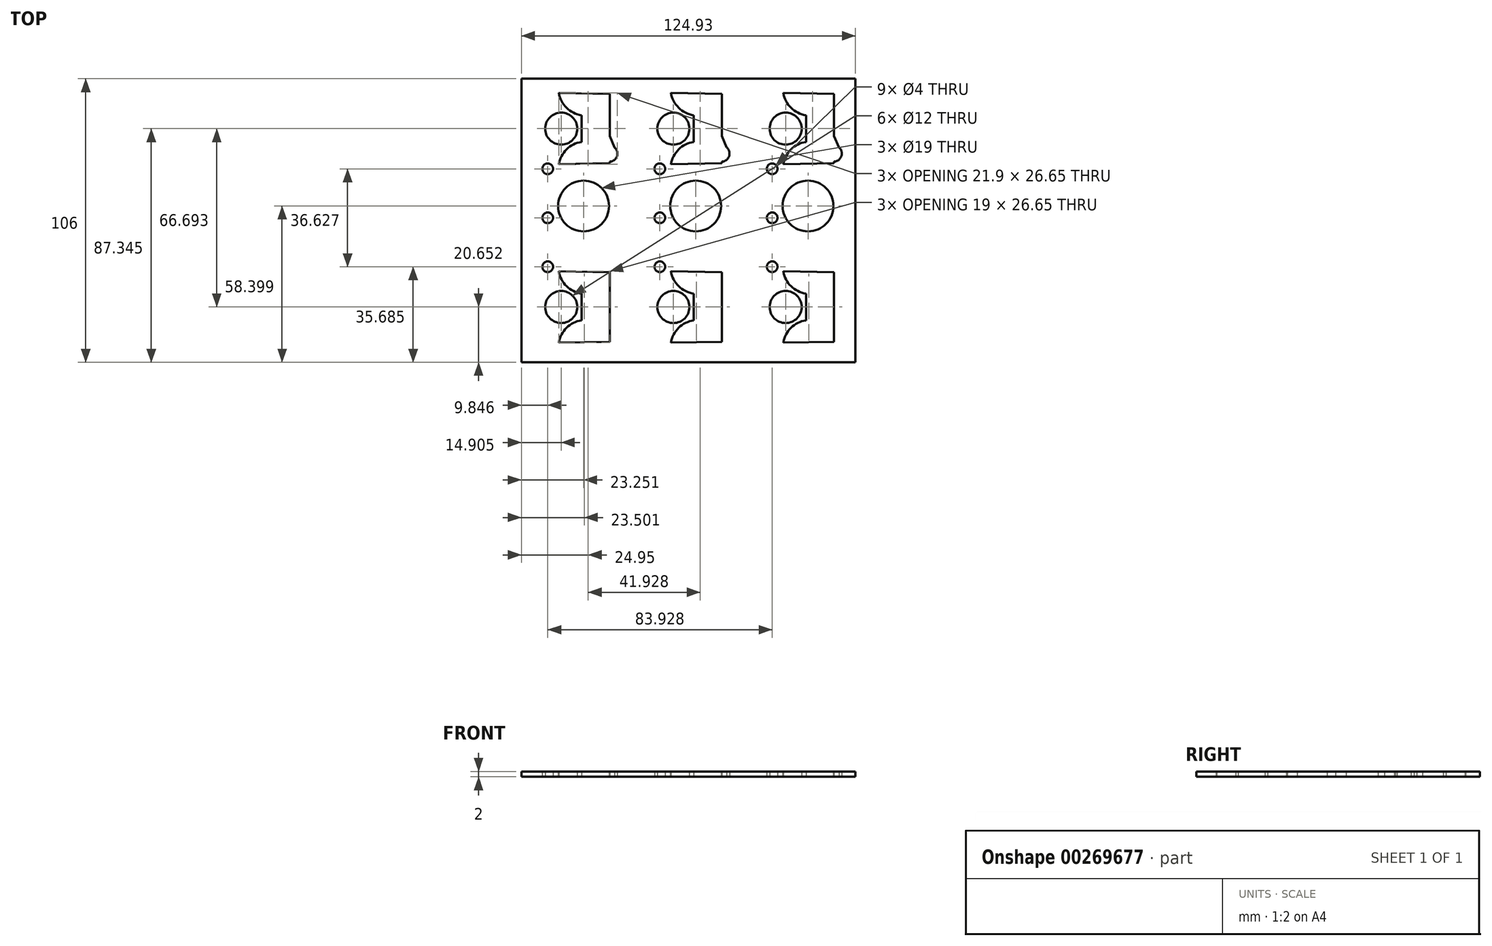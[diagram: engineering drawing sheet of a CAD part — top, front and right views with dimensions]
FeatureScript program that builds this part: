
annotation { "Feature Type Name" : "Feature", "Feature Type Description" : "" }
export const myFeature = defineFeature(function(context is Context, id is Id, definition is map)
    precondition{}
    {
        {
            var Q0;
            Q0=qCreatedBy(makeId("Top.planeOp"),FACE);
            var sketch = newSketch(context, id + "F0", { "sketchPlane" : qUnion([Q0])});
            skLineSegment(sketch, "E0.bottom", {"start": v(-21.33, 48.69) * mm, "end": v(19.67, 48.69) * mm});
            skLineSegment(sketch, "E0.top", {"start": v(-21.33, -57.31) * mm, "end": v(19.67, -57.31) * mm});
            skLineSegment(sketch, "E0.left", {"start": v(-21.33, 48.69) * mm, "end": v(-21.33, -57.31) * mm});
            skLineSegment(sketch, "E0.right", {"start": v(19.67, 48.69) * mm, "end": v(19.67, -57.31) * mm});
            skArc(sketch, "E1", {"start": v(-7.33, 43.36) * mm, "mid": v(-4.44, 37.81) * mm, "end": v(1.17, 35.04) * mm});
            skLineSegment(sketch, "E2", {"start": v(1.17, 35.04) * mm, "end": v(1.17, 25.04) * mm});
            skLineSegment(sketch, "E3", {"start": v(-11.51, 30.04) * mm, "end": v(22.8, 30.04) * mm, "construction": true});
            skArc(sketch, "E4.MirrorCS", {"start": v(-7.33, 16.71) * mm, "mid": v(-4.44, 22.26) * mm, "end": v(1.17, 25.04) * mm});
            skCircle(sketch, "E5", {"center": v(-1.94, 38.54) * mm, "radius": 1.5 * mm});
            skCircle(sketch, "E6.MirrorC", {"center": v(-1.94, 21.54) * mm, "radius": 1.5 * mm});
            skCircle(sketch, "E7", {"center": v(-6.43, 30.04) * mm, "radius": 6 * mm});
            skLineSegment(sketch, "E8", {"start": v(-27.8, -3.31) * mm, "end": v(21.21, -3.31) * mm, "construction": true});
            skCircle(sketch, "E9.MirrorC", {"center": v(-1.94, -28.16) * mm, "radius": 1.5 * mm});
            skArc(sketch, "E10.MirrorCS", {"start": v(-7.33, -23.33) * mm, "mid": v(-4.44, -28.88) * mm, "end": v(1.17, -31.66) * mm});
            skLineSegment(sketch, "E11.MirrorCS", {"start": v(1.17, -41.66) * mm, "end": v(1.17, -31.66) * mm});
            skArc(sketch, "E12.MirrorCS", {"start": v(-7.33, -49.98) * mm, "mid": v(-4.44, -44.43) * mm, "end": v(1.17, -41.66) * mm});
            skCircle(sketch, "E13.MirrorC", {"center": v(-1.94, -45.16) * mm, "radius": 1.5 * mm});
            skCircle(sketch, "E14.MirrorC", {"center": v(-6.43, -36.66) * mm, "radius": 6 * mm});
            skLineSegment(sketch, "E15", {"start": v(-4.58, -20.4) * mm, "end": v(-4.58, -51.53) * mm, "construction": true});
            skLineSegment(sketch, "E16", {"start": v(11.67, -23.7) * mm, "end": v(11.67, -49.7) * mm});
            skLineSegment(sketch, "E17", {"start": v(11.67, -49.7) * mm, "end": v(-7.33, -49.98) * mm});
            skLineSegment(sketch, "E18", {"start": v(11.67, -23.7) * mm, "end": v(-7.33, -23.33) * mm});
            skLineSegment(sketch, "E19.MirrorCS", {"start": v(11.67, 17.07) * mm, "end": v(-7.33, 16.71) * mm});
            skLineSegment(sketch, "E20.MirrorCS", {"start": v(11.67, 17.07) * mm, "end": v(11.67, 43.07) * mm});
            skLineSegment(sketch, "E21.MirrorCS", {"start": v(11.67, 43.07) * mm, "end": v(-7.33, 43.36) * mm});
            skCircle(sketch, "E22", {"center": v(1.92, 1.09) * mm, "radius": 9.5 * mm});
            skCircle(sketch, "E23", {"center": v(8.67, 26.69) * mm, "radius": 3 * mm});
            skCircle(sketch, "E24", {"center": v(11.57, 20.69) * mm, "radius": 3 * mm});
            skCircle(sketch, "E25", {"center": v(-11.49, -3.31) * mm, "radius": 2 * mm});
            skCircle(sketch, "E26", {"center": v(-11.49, -21.63) * mm, "radius": 2 * mm});
            skCircle(sketch, "E27.MirrorC", {"center": v(-11.49, 15) * mm, "radius": 2 * mm});
            skLineSegment(sketch, "E28", {"start": v(6.28, 24.87) * mm, "end": v(8.86, 19.4) * mm});
            skLineSegment(sketch, "E29", {"start": v(13.53, 22.96) * mm, "end": v(11.43, 27.87) * mm});
            skLineSegment(sketch, "E30.bottom", {"start": v(20.67, 48.69) * mm, "end": v(61.67, 48.69) * mm});
            skLineSegment(sketch, "E30.top", {"start": v(20.67, -57.31) * mm, "end": v(61.67, -57.31) * mm});
            skLineSegment(sketch, "E30.left", {"start": v(20.67, 48.69) * mm, "end": v(20.67, -57.31) * mm});
            skLineSegment(sketch, "E30.right", {"start": v(61.67, 48.69) * mm, "end": v(61.67, -57.31) * mm});
            skArc(sketch, "E31", {"start": v(34.67, 43.36) * mm, "mid": v(37.56, 37.81) * mm, "end": v(43.17, 35.04) * mm});
            skLineSegment(sketch, "E32", {"start": v(43.17, 35.04) * mm, "end": v(43.17, 25.04) * mm});
            skLineSegment(sketch, "E33", {"start": v(30.49, 30.04) * mm, "end": v(64.8, 30.04) * mm, "construction": true});
            skArc(sketch, "E34.MirrorCS", {"start": v(34.67, 16.71) * mm, "mid": v(37.56, 22.26) * mm, "end": v(43.17, 25.04) * mm});
            skCircle(sketch, "E35", {"center": v(40.06, 38.54) * mm, "radius": 1.5 * mm});
            skCircle(sketch, "E36.MirrorC", {"center": v(40.06, 21.54) * mm, "radius": 1.5 * mm});
            skCircle(sketch, "E37", {"center": v(35.57, 30.04) * mm, "radius": 6 * mm});
            skLineSegment(sketch, "E38", {"start": v(14.2, -3.31) * mm, "end": v(63.21, -3.31) * mm, "construction": true});
            skCircle(sketch, "E39.MirrorC", {"center": v(40.06, -28.16) * mm, "radius": 1.5 * mm});
            skArc(sketch, "E40.MirrorCS", {"start": v(34.67, -23.33) * mm, "mid": v(37.56, -28.88) * mm, "end": v(43.17, -31.66) * mm});
            skLineSegment(sketch, "E41.MirrorCS", {"start": v(43.17, -41.66) * mm, "end": v(43.17, -31.66) * mm});
            skArc(sketch, "E42.MirrorCS", {"start": v(34.67, -49.98) * mm, "mid": v(37.56, -44.43) * mm, "end": v(43.17, -41.66) * mm});
            skCircle(sketch, "E43.MirrorC", {"center": v(40.06, -45.16) * mm, "radius": 1.5 * mm});
            skCircle(sketch, "E44.MirrorC", {"center": v(35.57, -36.66) * mm, "radius": 6 * mm});
            skLineSegment(sketch, "E45", {"start": v(37.42, -20.4) * mm, "end": v(37.42, -51.53) * mm, "construction": true});
            skLineSegment(sketch, "E46", {"start": v(53.67, -23.7) * mm, "end": v(53.67, -49.7) * mm});
            skLineSegment(sketch, "E47", {"start": v(53.67, -49.7) * mm, "end": v(34.67, -49.98) * mm});
            skLineSegment(sketch, "E48", {"start": v(53.67, -23.7) * mm, "end": v(34.67, -23.33) * mm});
            skLineSegment(sketch, "E49.MirrorCS", {"start": v(53.67, 17.07) * mm, "end": v(34.67, 16.71) * mm});
            skLineSegment(sketch, "E50.MirrorCS", {"start": v(53.67, 17.07) * mm, "end": v(53.67, 43.07) * mm});
            skLineSegment(sketch, "E51.MirrorCS", {"start": v(53.67, 43.07) * mm, "end": v(34.67, 43.36) * mm});
            skCircle(sketch, "E52", {"center": v(43.92, 1.09) * mm, "radius": 9.5 * mm});
            skCircle(sketch, "E53", {"center": v(50.67, 26.69) * mm, "radius": 3 * mm});
            skCircle(sketch, "E54", {"center": v(53.57, 20.69) * mm, "radius": 3 * mm});
            skCircle(sketch, "E55", {"center": v(30.51, -3.31) * mm, "radius": 2 * mm});
            skCircle(sketch, "E56", {"center": v(30.51, -21.63) * mm, "radius": 2 * mm});
            skCircle(sketch, "E57.MirrorC", {"center": v(30.51, 15) * mm, "radius": 2 * mm});
            skLineSegment(sketch, "E58", {"start": v(48.28, 24.87) * mm, "end": v(50.86, 19.4) * mm});
            skLineSegment(sketch, "E59", {"start": v(55.53, 22.96) * mm, "end": v(53.43, 27.87) * mm});
            skLineSegment(sketch, "E60.bottom", {"start": v(-63.26, 48.69) * mm, "end": v(-22.26, 48.69) * mm});
            skLineSegment(sketch, "E60.top", {"start": v(-63.26, -57.31) * mm, "end": v(-22.26, -57.31) * mm});
            skLineSegment(sketch, "E60.left", {"start": v(-63.26, 48.69) * mm, "end": v(-63.26, -57.31) * mm});
            skLineSegment(sketch, "E60.right", {"start": v(-22.26, 48.69) * mm, "end": v(-22.26, -57.31) * mm});
            skArc(sketch, "E61", {"start": v(-49.26, 43.36) * mm, "mid": v(-46.37, 37.81) * mm, "end": v(-40.76, 35.04) * mm});
            skLineSegment(sketch, "E62", {"start": v(-40.76, 35.04) * mm, "end": v(-40.76, 25.04) * mm});
            skLineSegment(sketch, "E63", {"start": v(-53.44, 30.04) * mm, "end": v(-19.13, 30.04) * mm, "construction": true});
            skArc(sketch, "E64.MirrorCS", {"start": v(-49.26, 16.71) * mm, "mid": v(-46.37, 22.26) * mm, "end": v(-40.76, 25.04) * mm});
            skCircle(sketch, "E65", {"center": v(-43.87, 38.54) * mm, "radius": 1.5 * mm});
            skCircle(sketch, "E66.MirrorC", {"center": v(-43.87, 21.54) * mm, "radius": 1.5 * mm});
            skCircle(sketch, "E67", {"center": v(-48.35, 30.04) * mm, "radius": 6 * mm});
            skLineSegment(sketch, "E68", {"start": v(-69.73, -3.31) * mm, "end": v(-20.72, -3.31) * mm, "construction": true});
            skCircle(sketch, "E69.MirrorC", {"center": v(-43.87, -28.16) * mm, "radius": 1.5 * mm});
            skArc(sketch, "E70.MirrorCS", {"start": v(-49.26, -23.33) * mm, "mid": v(-46.37, -28.88) * mm, "end": v(-40.76, -31.66) * mm});
            skLineSegment(sketch, "E71.MirrorCS", {"start": v(-40.76, -41.66) * mm, "end": v(-40.76, -31.66) * mm});
            skArc(sketch, "E72.MirrorCS", {"start": v(-49.26, -49.98) * mm, "mid": v(-46.37, -44.43) * mm, "end": v(-40.76, -41.66) * mm});
            skCircle(sketch, "E73.MirrorC", {"center": v(-43.87, -45.16) * mm, "radius": 1.5 * mm});
            skCircle(sketch, "E74.MirrorC", {"center": v(-48.35, -36.66) * mm, "radius": 6 * mm});
            skLineSegment(sketch, "E75", {"start": v(-46.5, -20.4) * mm, "end": v(-46.5, -51.53) * mm, "construction": true});
            skLineSegment(sketch, "E76", {"start": v(-30.26, -23.7) * mm, "end": v(-30.26, -49.7) * mm});
            skLineSegment(sketch, "E77", {"start": v(-30.26, -49.7) * mm, "end": v(-49.26, -49.98) * mm});
            skLineSegment(sketch, "E78", {"start": v(-30.26, -23.7) * mm, "end": v(-49.26, -23.33) * mm});
            skLineSegment(sketch, "E79.MirrorCS", {"start": v(-30.26, 17.07) * mm, "end": v(-49.26, 16.71) * mm});
            skLineSegment(sketch, "E80.MirrorCS", {"start": v(-30.26, 17.07) * mm, "end": v(-30.26, 43.07) * mm});
            skLineSegment(sketch, "E81.MirrorCS", {"start": v(-30.26, 43.07) * mm, "end": v(-49.26, 43.36) * mm});
            skCircle(sketch, "E82", {"center": v(-40, 1.09) * mm, "radius": 9.5 * mm});
            skCircle(sketch, "E83", {"center": v(-33.26, 26.69) * mm, "radius": 3 * mm});
            skCircle(sketch, "E84", {"center": v(-30.36, 20.69) * mm, "radius": 3 * mm});
            skCircle(sketch, "E85", {"center": v(-53.41, -3.31) * mm, "radius": 2 * mm});
            skCircle(sketch, "E86", {"center": v(-53.41, -21.63) * mm, "radius": 2 * mm});
            skCircle(sketch, "E87.MirrorC", {"center": v(-53.41, 15) * mm, "radius": 2 * mm});
            skLineSegment(sketch, "E88", {"start": v(-35.65, 24.87) * mm, "end": v(-33.07, 19.4) * mm});
            skLineSegment(sketch, "E89", {"start": v(-28.4, 22.96) * mm, "end": v(-30.5, 27.87) * mm});
            skLineSegment(sketch, "E90", {"start": v(-22.26, -57.31) * mm, "end": v(-21.33, -57.31) * mm});
            skLineSegment(sketch, "E91", {"start": v(19.67, -57.31) * mm, "end": v(20.67, -57.31) * mm});
            skLineSegment(sketch, "E92", {"start": v(-22.26, 48.69) * mm, "end": v(-21.33, 48.69) * mm});
            skLineSegment(sketch, "E93", {"start": v(19.67, 48.69) * mm, "end": v(20.67, 48.69) * mm});
            skSolve(sketch);
        }
        {
            var Q0;
            Q0=makeQuery(id+"F0.imprint","IMPRINT",FACE,{"disambiguationData":[TD([[makeQuery(id+"F0.imprint","IMPRINT",EDGE,{"derivedFrom":sQuery(id+"F0.wireOp",EDGE,"E60.bottom")}),-1.0]])]});
            var Q1;
            Q1=makeQuery(id+"F0.imprint","IMPRINT",FACE,{"disambiguationData":[TD([[makeQuery(id+"F0.imprint","IMPRINT",EDGE,{"derivedFrom":sQuery(id+"F0.wireOp",EDGE,"E0.left")}),-1.0]])]});
            var Q2;
            Q2=makeQuery(id+"F0.imprint","IMPRINT",FACE,{"disambiguationData":[TD([[makeQuery(id+"F0.imprint","IMPRINT",EDGE,{"derivedFrom":sQuery(id+"F0.wireOp",EDGE,"E0.bottom")}),-1.0]])]});
            var Q3;
            Q3=makeQuery(id+"F0.imprint","IMPRINT",FACE,{"disambiguationData":[TD([[makeQuery(id+"F0.imprint","IMPRINT",EDGE,{"derivedFrom":sQuery(id+"F0.wireOp",EDGE,"E0.right")}),1.0]])]});
            var Q4;
            Q4=makeQuery(id+"F0.imprint","IMPRINT",FACE,{"disambiguationData":[TD([[makeQuery(id+"F0.imprint","IMPRINT",EDGE,{"derivedFrom":sQuery(id+"F0.wireOp",EDGE,"E30.bottom")}),-1.0]])]});
            extrude(context, id + "F1", {"entities" : qUnion([Q0, Q1, Q2, Q3, Q4]), "depth" : 2 * mm});
        }
    });
